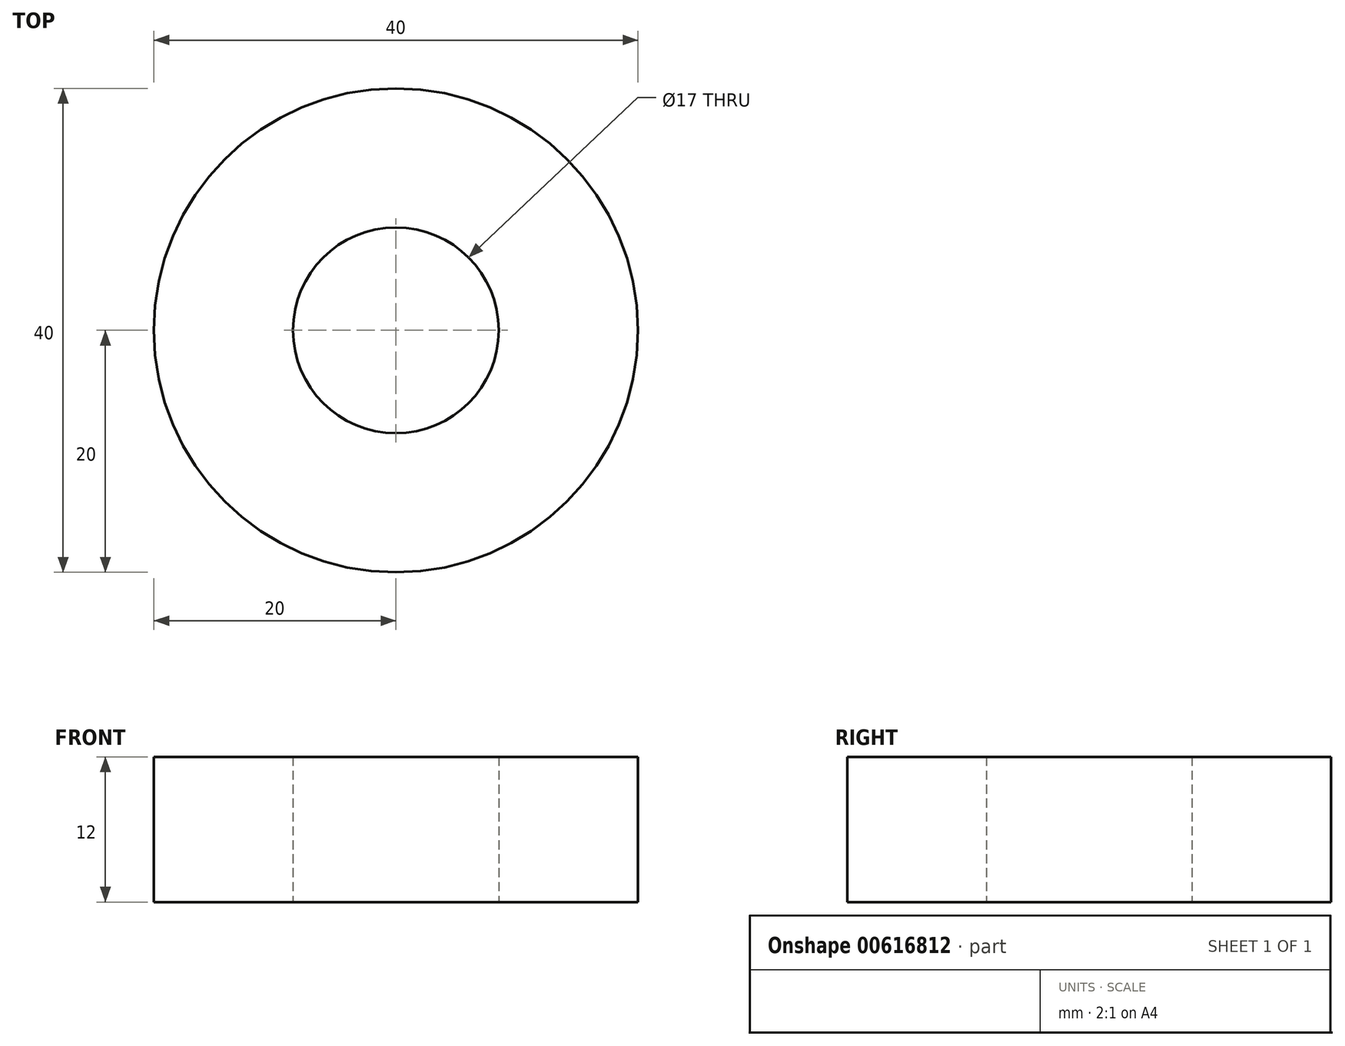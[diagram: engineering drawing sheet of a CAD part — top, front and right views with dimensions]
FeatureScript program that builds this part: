
annotation { "Feature Type Name" : "Feature", "Feature Type Description" : "" }
export const myFeature = defineFeature(function(context is Context, id is Id, definition is map)
    precondition{}
    {
        {
            var Q0;
            Q0=qCreatedBy(makeId("Top.planeOp"),FACE);
            var sketch = newSketch(context, id + "F0", { "sketchPlane" : qUnion([Q0])});
            skCircle(sketch, "E0", {"center": v(0, 0) * mm, "radius": 20 * mm});
            skCircle(sketch, "E1", {"center": v(0, 0) * mm, "radius": 8.5 * mm});
            skSolve(sketch);
        }
        {
            var Q0;
            Q0=makeQuery(id+"F0.imprint","IMPRINT",FACE,{"disambiguationData":[TD([[makeQuery(id+"F0.imprint","IMPRINT",EDGE,{"derivedFrom":sQuery(id+"F0.wireOp",EDGE,"E0")}),1.0]])]});
            extrude(context, id + "F1", {"entities" : qUnion([Q0]), "depth" : 12 * mm, "offsetDistance" : 25 * mm});
        }
    });
